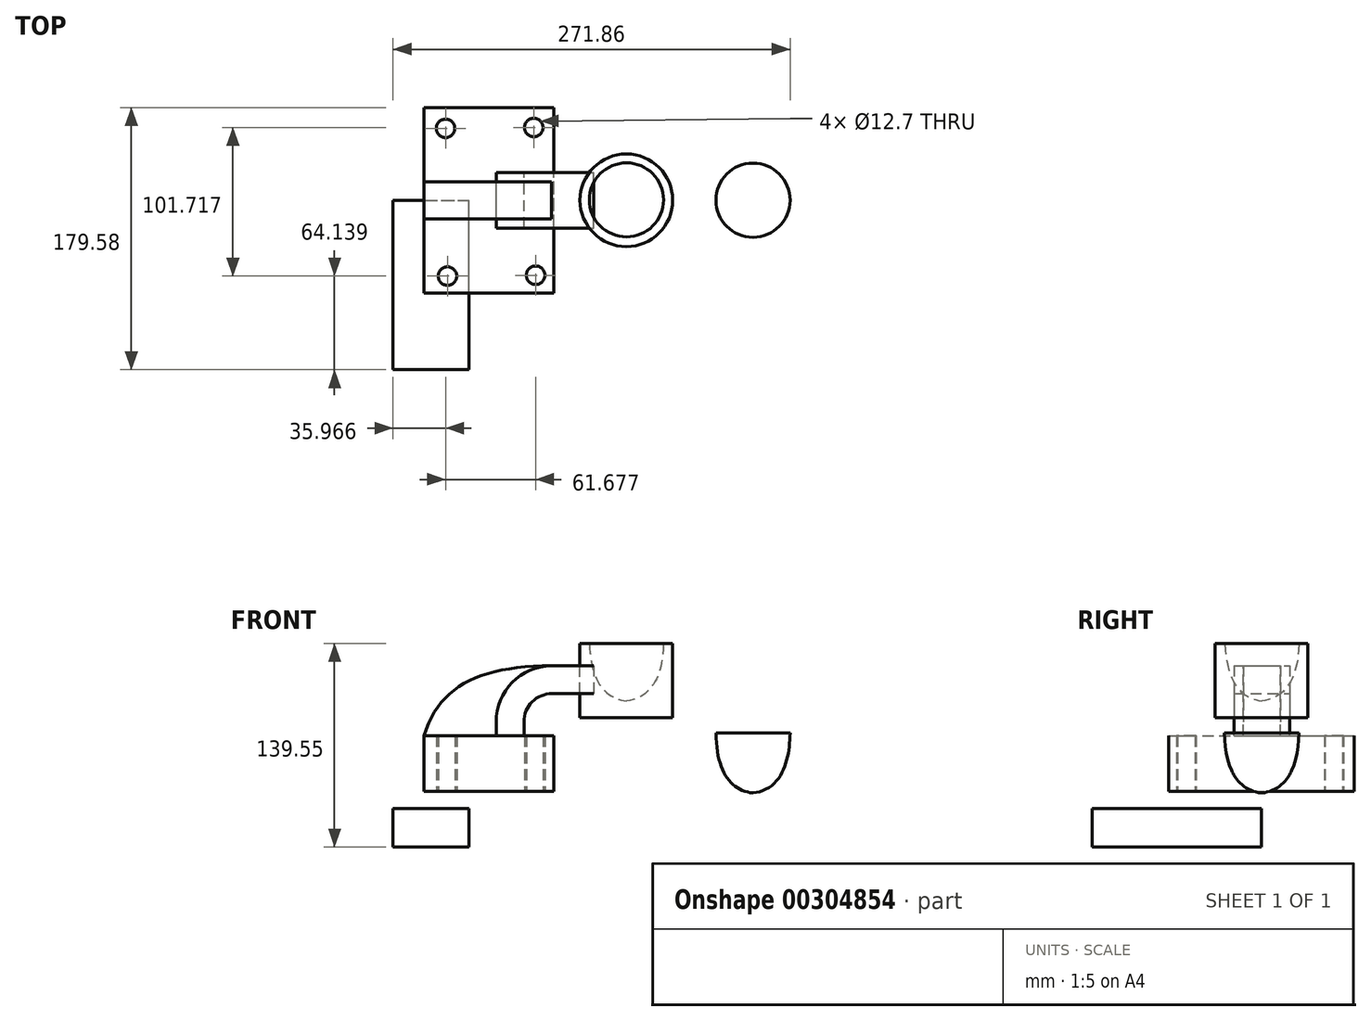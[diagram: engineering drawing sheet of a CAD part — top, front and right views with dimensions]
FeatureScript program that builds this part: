
annotation { "Feature Type Name" : "Feature", "Feature Type Description" : "" }
export const myFeature = defineFeature(function(context is Context, id is Id, definition is map)
    precondition{}
    {
        {
            var Q0;
            Q0=qCreatedBy(makeId("Front.planeOp"),FACE);
            var sketch = newSketch(context, id + "F0", { "sketchPlane" : qUnion([Q0])});
            skLineSegment(sketch, "E0.bottom", {"start": v(-41.56, 24.86) * mm, "end": v(47.34, 24.86) * mm});
            skLineSegment(sketch, "E0.top", {"start": v(-41.56, -13.24) * mm, "end": v(47.34, -13.24) * mm});
            skLineSegment(sketch, "E0.left", {"start": v(-41.56, 24.86) * mm, "end": v(-41.56, -13.24) * mm});
            skLineSegment(sketch, "E0.right", {"start": v(47.34, 24.86) * mm, "end": v(47.34, -13.24) * mm});
            skLineSegment(sketch, "E1.bottom", {"start": v(96.92, 88.06) * mm, "end": v(128.67, 88.06) * mm});
            skLineSegment(sketch, "E1.top", {"start": v(96.92, 37.26) * mm, "end": v(128.67, 37.26) * mm});
            skLineSegment(sketch, "E1.left", {"start": v(96.92, 88.06) * mm, "end": v(96.92, 37.26) * mm});
            skLineSegment(sketch, "E1.right", {"start": v(128.67, 88.06) * mm, "end": v(128.67, 37.26) * mm});
            skLineSegment(sketch, "E2", {"start": v(26.76, 24.86) * mm, "end": v(26.76, 34.36) * mm});
            skLineSegment(sketch, "E3", {"start": v(46.2, 53.8) * mm, "end": v(74.58, 53.8) * mm});
            skArc(sketch, "E4", {"start": v(26.76, 34.36) * mm, "mid": v(32.45, 48.1) * mm, "end": v(46.2, 53.8) * mm});
            skArc(sketch, "E5.0", {"start": v(7.71, 34.36) * mm, "mid": v(18.98, 61.57) * mm, "end": v(46.2, 72.84) * mm});
            skLineSegment(sketch, "E6.0", {"start": v(7.71, 24.86) * mm, "end": v(7.71, 34.36) * mm});
            skLineSegment(sketch, "E7.0", {"start": v(46.2, 72.84) * mm, "end": v(74.58, 72.84) * mm});
            skFitSpline(sketch, "E8", {"points": [v(-41.56, 24.86) * mm, v(46.2, 72.84) * mm], "startDerivative": vector(31.3, 103.6) * mm, "endDerivative": vector(148, 0.92) * mm});
            skLineSegment(sketch, "E9", {"start": v(74.58, 72.84) * mm, "end": v(74.58, 53.8) * mm});
            skFitSpline(sketch, "E10", {"points": [v(158.22, 26.6) * mm, v(183.62, -14.34) * mm], "startDerivative": vector(1.2, -79.79) * mm, "endDerivative": vector(45.3, -4.77) * mm});
            skLineSegment(sketch, "E11", {"start": v(183.62, -14.34) * mm, "end": v(183.62, 26.6) * mm});
            skLineSegment(sketch, "E12", {"start": v(158.22, 26.6) * mm, "end": v(183.62, 26.6) * mm});
            skSolve(sketch);
        }
        {
            var Q0;
            Q0=makeQuery(id+"F0.imprint","IMPRINT",FACE,{"disambiguationData":[TD([[makeQuery(id+"F0.imprint","IMPRINT",EDGE,{"derivedFrom":sQuery(id+"F0.wireOp",EDGE,"E0.top")}),1.0]])]});
            extrude(context, id + "F1", {"entities" : qUnion([Q0]), "endBound" : BoundingType.SYMMETRIC, "depth" : 127 * mm});
        }
        {
            var Q0;
            {var subQ3=sQuery(id+"F0.wireOp",EDGE,"E6.0");Q0=makeQuery(id+"F0.imprint","IMPRINT",FACE,{"disambiguationData":[TD([[makeQuery(id+"F0.imprint","IMPRINT",EDGE,{"derivedFrom":subQ3}),1.0]])]});}
            extrude(context, id + "F2", {"entities" : qUnion([Q0]), "operationType" : NewBodyOperationType.ADD, "endBound" : BoundingType.SYMMETRIC, "depth" : 25.4 * mm});
        }
        {
            var Q0;
            Q0=makeQuery(id+"F0.imprint","IMPRINT",FACE,{"disambiguationData":[TD([[makeQuery(id+"F0.imprint","IMPRINT",EDGE,{"derivedFrom":sQuery(id+"F0.wireOp",EDGE,"E1.bottom")}),-1.0]])]});
            var Q1;
            Q1=sQuery(id+"F0.wireOp",EDGE,"E1.left");
            revolve(context, id + "F3", {"entities" : qUnion([Q0]), "axis" : qUnion([Q1]), "revolveType" : RevolveType.FULL});
        }
        {
            var Q0;
            {var subQ0=sQuery(id+"F0.wireOp",EDGE,"E2");Q0=makeQuery(id+"F0.imprint","IMPRINT",FACE,{"disambiguationData":[TD([[makeQuery(id+"F0.imprint","IMPRINT",EDGE,{"derivedFrom":subQ0}),1.0]])]});}
            extrude(context, id + "F4", {"entities" : qUnion([Q0]), "endBound" : BoundingType.SYMMETRIC, "depth" : 38.1 * mm});
        }
        {
            var Q0;
            Q0=makeQuery(id+"F0.imprint","IMPRINT",FACE,{"disambiguationData":[TD([[makeQuery(id+"F0.imprint","IMPRINT",EDGE,{"derivedFrom":sQuery(id+"F0.wireOp",EDGE,"E10")}),1.0]])]});
            var Q1;
            Q1=sQuery(id+"F0.wireOp",EDGE,"E11");
            revolve(context, id + "F5", {"entities" : qUnion([Q0]), "axis" : qUnion([Q1]), "revolveType" : RevolveType.FULL});
        }
        {
            var Q0;
            Q0=makeQuery(id+"F5.opRevolve","SWEPT_BODY",BODY,{"disambiguationData":[OSD([sQuery(id+"F0.wireOp",EDGE,"E10"),sQuery(id+"F0.wireOp",EDGE,"E11"),sQuery(id+"F0.wireOp",EDGE,"E12")])]});
            transform(context, id + "F6", {"entities" : qUnion([Q0]), "transformType" : TransformType.TRANSLATION_3D, "dx" : -86.61 * mm, "dy" : 0.25 * mm, "dz" : 63 * mm, "makeCopy" : true});
        }
        {
            var Q0;
            Q0=makeQuery(id+"F6.opPattern","COPY",BODY,{"derivedFrom":makeQuery(id+"F5.opRevolve","SWEPT_BODY",BODY,{"disambiguationData":[OSD([sQuery(id+"F0.wireOp",EDGE,"E10"),sQuery(id+"F0.wireOp",EDGE,"E11"),sQuery(id+"F0.wireOp",EDGE,"E12")])]}),"instanceName":"1"});
            var Q1;
            Q1=makeQuery(id+"F3.opRevolve","SWEPT_BODY",BODY,{"disambiguationData":[OSD([sQuery(id+"F0.wireOp",EDGE,"E1.bottom"),sQuery(id+"F0.wireOp",EDGE,"E1.top"),sQuery(id+"F0.wireOp",EDGE,"E1.left"),sQuery(id+"F0.wireOp",EDGE,"E1.right")])]});
            booleanBodies(context, id + "F7", {"operationType" : BooleanOperationType.SUBTRACTION, "tools" : qUnion([Q0]), "targets" : qUnion([Q1])});
        }
        {
            var Q0;
            Q0=qCreatedBy(makeId("Top.planeOp"),FACE);
            var sketch = newSketch(context, id + "F8", { "sketchPlane" : qUnion([Q0])});
            skCircle(sketch, "E13", {"center": v(-26.87, 49.22) * mm, "radius": 6.35 * mm});
            skCircle(sketch, "E14", {"center": v(33.51, 49.78) * mm, "radius": 6.35 * mm});
            skCircle(sketch, "E15", {"center": v(-25.58, -51.94) * mm, "radius": 6.35 * mm});
            skCircle(sketch, "E16", {"center": v(34.8, -51.39) * mm, "radius": 6.35 * mm});
            skSolve(sketch);
        }
        {
            var Q0;
            Q0 = qSketchRegion(id + "F8", true);
            extrude(context, id + "F9", {"entities" : qUnion([Q0]), "endBound" : BoundingType.SYMMETRIC, "depth" : 76.2 * mm});
        }
        {
            var Q0;
            Q0=makeQuery(id+"F9.opExtrude","SWEPT_BODY",BODY,{"disambiguationData":[OSD([sQuery(id+"F8.wireOp",EDGE,"E15")])]});
            var Q1;
            Q1=makeQuery(id+"F9.opExtrude","SWEPT_BODY",BODY,{"disambiguationData":[OSD([sQuery(id+"F8.wireOp",EDGE,"E16")])]});
            var Q2;
            Q2=makeQuery(id+"F9.opExtrude","SWEPT_BODY",BODY,{"disambiguationData":[OSD([sQuery(id+"F8.wireOp",EDGE,"E13")])]});
            var Q3;
            Q3=makeQuery(id+"F9.opExtrude","SWEPT_BODY",BODY,{"disambiguationData":[OSD([sQuery(id+"F8.wireOp",EDGE,"E14")])]});
            var Q4;
            Q4=makeQuery(id+"F1.opExtrude","SWEPT_BODY",BODY,{"disambiguationData":[OSD([sQuery(id+"F0.wireOp",EDGE,"E0.bottom"),sQuery(id+"F0.wireOp",EDGE,"E0.top"),sQuery(id+"F0.wireOp",EDGE,"E0.left"),sQuery(id+"F0.wireOp",EDGE,"E0.right")])]});
            booleanBodies(context, id + "F10", {"operationType" : BooleanOperationType.SUBTRACTION, "tools" : qUnion([Q0, Q1, Q2, Q3]), "targets" : qUnion([Q4])});
        }
        {
            var Q0;
            Q0=qCreatedBy(makeId("Front.planeOp"),FACE);
            var sketch = newSketch(context, id + "F11", { "sketchPlane" : qUnion([Q0])});
            skLineSegment(sketch, "E17.bottom", {"start": v(-62.84, -24.94) * mm, "end": v(-10.98, -24.94) * mm});
            skLineSegment(sketch, "E17.top", {"start": v(-62.84, -51.5) * mm, "end": v(-10.98, -51.5) * mm});
            skLineSegment(sketch, "E17.left", {"start": v(-62.84, -24.94) * mm, "end": v(-62.84, -51.5) * mm});
            skLineSegment(sketch, "E17.right", {"start": v(-10.98, -24.94) * mm, "end": v(-10.98, -51.5) * mm});
            skSolve(sketch);
        }
        {
            var Q0;
            Q0 = qSketchRegion(id + "F11", true);
            extrude(context, id + "F12", {"entities" : qUnion([Q0]), "depth" : 116.08 * mm});
        }
    });
